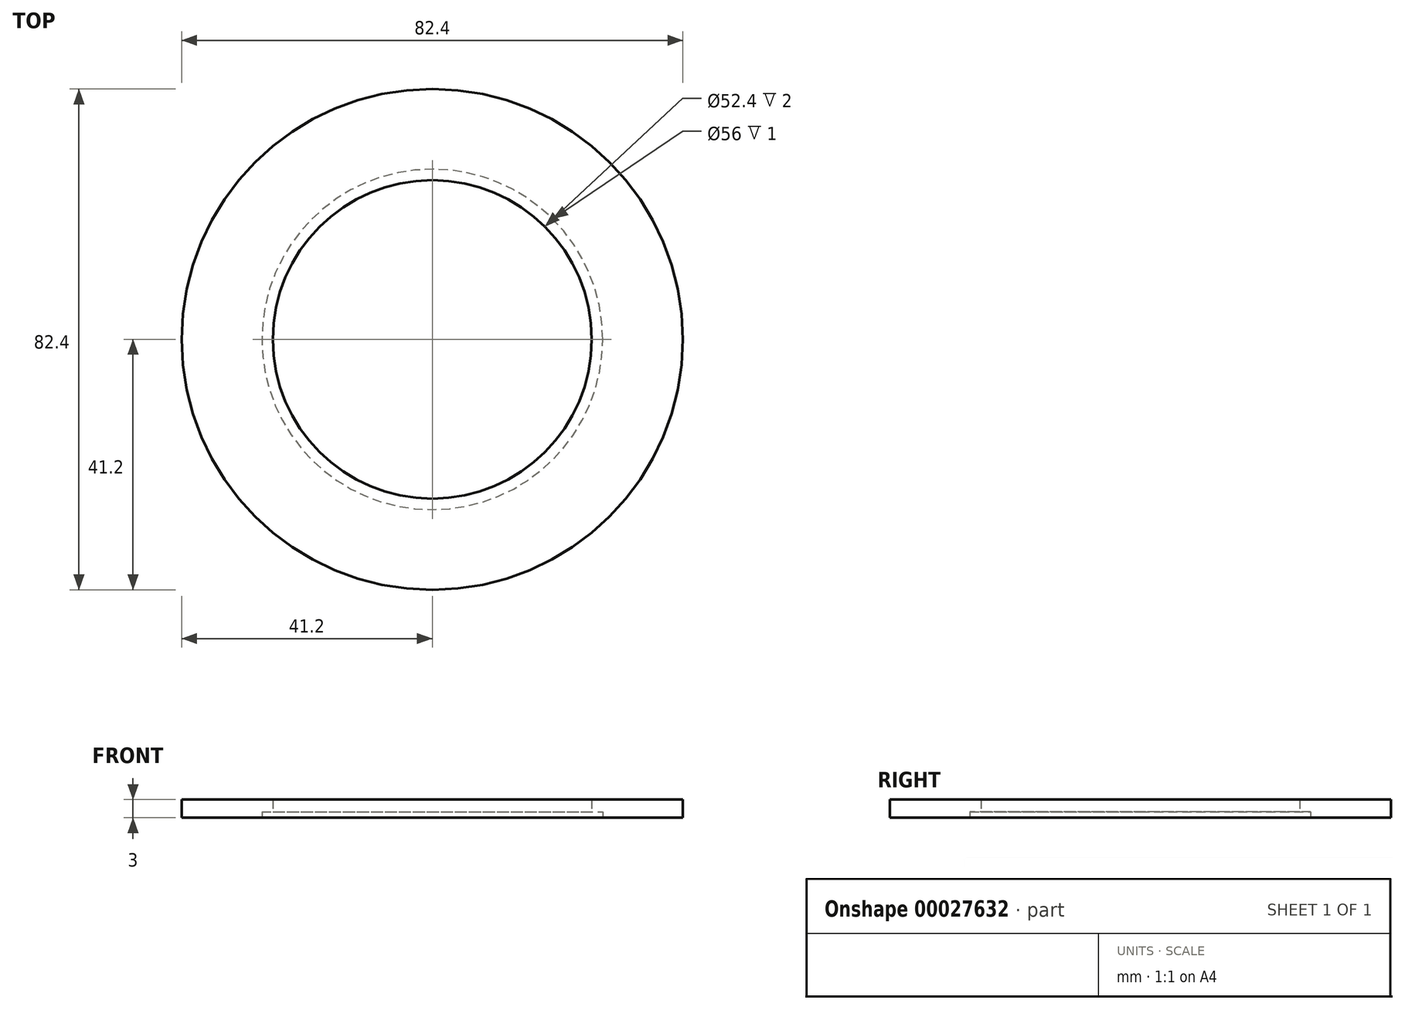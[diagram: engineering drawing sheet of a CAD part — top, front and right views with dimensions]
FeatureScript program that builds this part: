
annotation { "Feature Type Name" : "Feature", "Feature Type Description" : "" }
export const myFeature = defineFeature(function(context is Context, id is Id, definition is map)
    precondition{}
    {
        {
            var Q0;
            Q0=qCreatedBy(makeId("Front.planeOp"),FACE);
            var sketch = newSketch(context, id + "F0", { "sketchPlane" : qUnion([Q0])});
            skLineSegment(sketch, "E0", {"start": v(0, 0) * mm, "end": v(0, 5) * mm});
            skLineSegment(sketch, "E1", {"start": v(28, 0) * mm, "end": v(28, 1) * mm});
            skLineSegment(sketch, "E2", {"start": v(28, 1) * mm, "end": v(26.2, 1) * mm});
            skLineSegment(sketch, "E3", {"start": v(26.2, 1) * mm, "end": v(26.2, 3) * mm});
            skLineSegment(sketch, "E4", {"start": v(26.2, 3) * mm, "end": v(41.2, 3) * mm});
            skLineSegment(sketch, "E5", {"start": v(41.2, 3) * mm, "end": v(41.2, 0) * mm});
            skLineSegment(sketch, "E6", {"start": v(41.2, 0) * mm, "end": v(28, 0) * mm});
            skLineSegment(sketch, "E7.bottom", {"start": v(41.2, 0) * mm, "end": v(39.02, 0) * mm});
            skLineSegment(sketch, "E7.top", {"start": v(41.2, -2.61) * mm, "end": v(39.02, -2.61) * mm});
            skLineSegment(sketch, "E7.left", {"start": v(41.2, 0) * mm, "end": v(41.2, -2.61) * mm});
            skLineSegment(sketch, "E7.right", {"start": v(39.02, 0) * mm, "end": v(39.02, -2.61) * mm});
            skSolve(sketch);
        }
        {
            var Q0;
            Q0=makeQuery(id+"F0.imprint","IMPRINT",FACE,{"disambiguationData":[TD([[makeQuery(id+"F0.imprint","IMPRINT",EDGE,{"derivedFrom":sQuery(id+"F0.wireOp",EDGE,"E1")}),-1.0]])]});
            var Q1;
            Q1=sQuery(id+"F0.wireOp",EDGE,"E0");
            revolve(context, id + "F1", {"entities" : qUnion([Q0]), "axis" : qUnion([Q1]), "revolveType" : RevolveType.FULL});
        }
        {
            var Q0;
            Q0=makeQuery(id+"F1.opRevolve","SWEPT_BODY",BODY,{"disambiguationData":[OSD([sQuery(id+"F0.wireOp",EDGE,"E1"),sQuery(id+"F0.wireOp",EDGE,"E2"),sQuery(id+"F0.wireOp",EDGE,"E3"),sQuery(id+"F0.wireOp",EDGE,"E4"),sQuery(id+"F0.wireOp",EDGE,"E5"),sQuery(id+"F0.wireOp",EDGE,"E6")])]});
            deleteBodies(context, id + "F2", {"entities" : qUnion([Q0])});
        }
        {
            var Q0;
            Q0=makeQuery(id+"F0.imprint","IMPRINT",FACE,{"disambiguationData":[TD([[makeQuery(id+"F0.imprint","IMPRINT",EDGE,{"derivedFrom":sQuery(id+"F0.wireOp",EDGE,"E1")}),-1.0]])]});
            var Q1;
            Q1=sQuery(id+"F0.wireOp",EDGE,"E0");
            revolve(context, id + "F3", {"entities" : qUnion([Q0]), "axis" : qUnion([Q1]), "revolveType" : RevolveType.FULL});
        }
        {
            var Q0;
            Q0=makeQuery(id+"F3.opRevolve","SWEPT_BODY",BODY,{"disambiguationData":[OSD([sQuery(id+"F0.wireOp",EDGE,"E1"),sQuery(id+"F0.wireOp",EDGE,"E2"),sQuery(id+"F0.wireOp",EDGE,"E3"),sQuery(id+"F0.wireOp",EDGE,"E4"),sQuery(id+"F0.wireOp",EDGE,"E5"),sQuery(id+"F0.wireOp",EDGE,"E6")])]});
            deleteBodies(context, id + "F4", {"entities" : qUnion([Q0])});
        }
        {
            var Q0;
            Q0=makeQuery(id+"F0.imprint","IMPRINT",FACE,{"disambiguationData":[TD([[makeQuery(id+"F0.imprint","IMPRINT",EDGE,{"derivedFrom":sQuery(id+"F0.wireOp",EDGE,"E1")}),-1.0]])]});
            var Q1;
            Q1=makeQuery(id+"F0.imprint","IMPRINT",FACE,{"disambiguationData":[TD([[makeQuery(id+"F0.imprint","IMPRINT",EDGE,{"derivedFrom":sQuery(id+"F0.wireOp",EDGE,"E7.bottom")}),1.0]])]});
            var Q2;
            Q2=sQuery(id+"F0.wireOp",EDGE,"E0");
            revolve(context, id + "F5", {"entities" : qUnion([Q0, Q1]), "axis" : qUnion([Q2]), "revolveType" : RevolveType.FULL});
        }
    });
